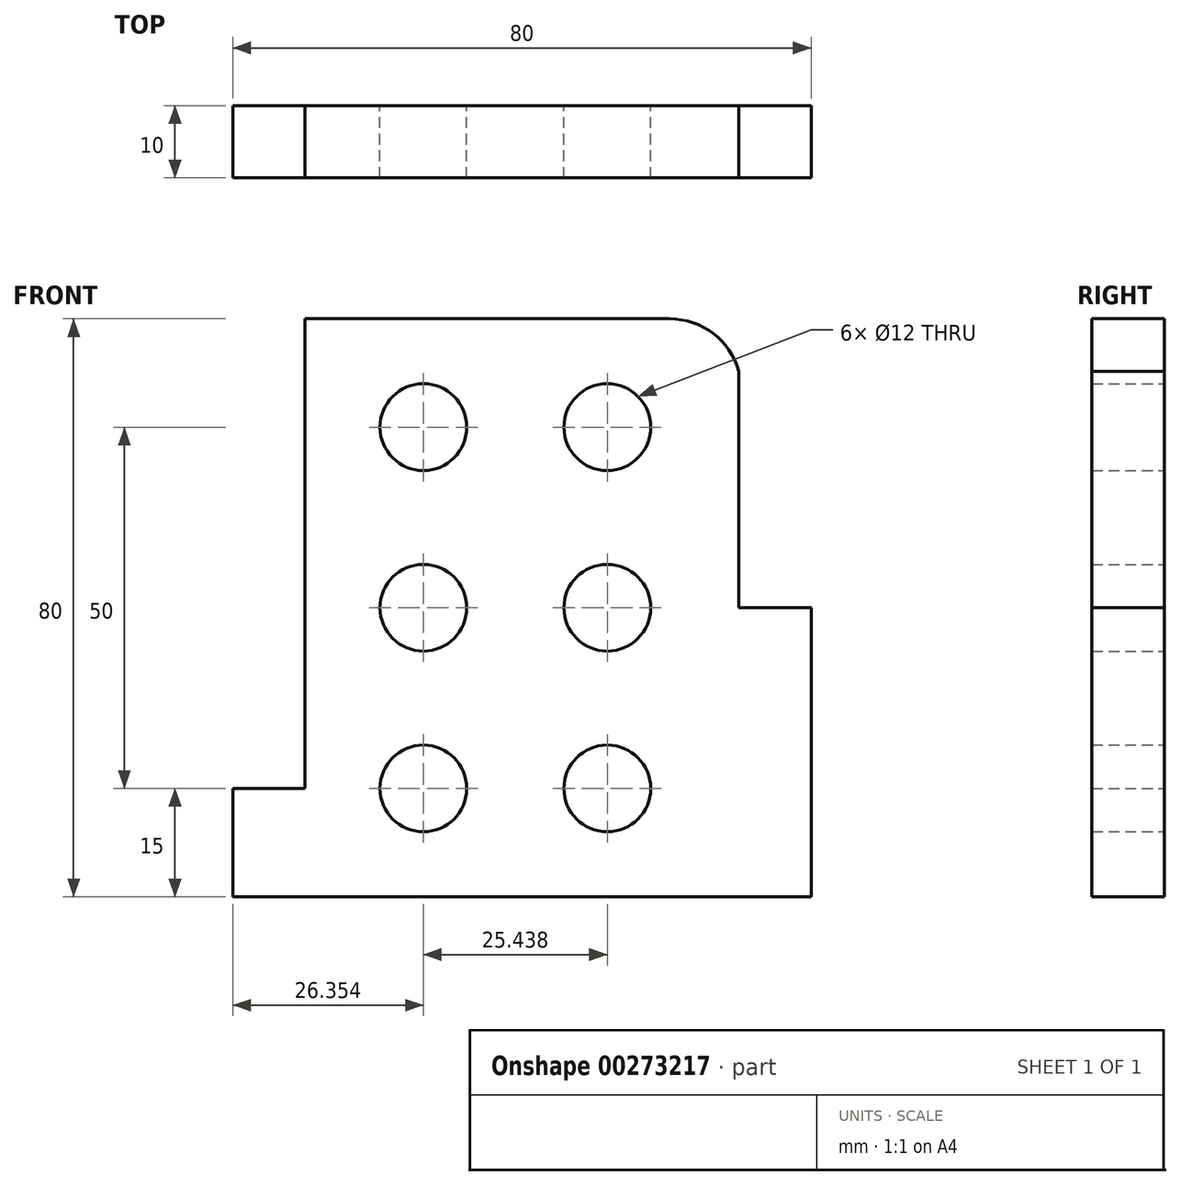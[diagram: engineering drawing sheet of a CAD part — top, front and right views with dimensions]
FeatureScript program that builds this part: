
annotation { "Feature Type Name" : "Feature", "Feature Type Description" : "" }
export const myFeature = defineFeature(function(context is Context, id is Id, definition is map)
    precondition{}
    {
        {
            var Q0;
            Q0=qCreatedBy(makeId("Front.planeOp"),FACE);
            var sketch = newSketch(context, id + "F0", { "sketchPlane" : qUnion([Q0])});
            skLineSegment(sketch, "E0", {"start": v(10, 80) * mm, "end": v(10, 15) * mm});
            skLineSegment(sketch, "E1", {"start": v(10, 15) * mm, "end": v(0, 15) * mm});
            skLineSegment(sketch, "E2", {"start": v(0, 15) * mm, "end": v(0, 0) * mm});
            skLineSegment(sketch, "E3", {"start": v(70, 40) * mm, "end": v(80, 40) * mm});
            skLineSegment(sketch, "E4", {"start": v(0, 0) * mm, "end": v(80, 0) * mm});
            skLineSegment(sketch, "E5", {"start": v(80, 0) * mm, "end": v(80, 40) * mm});
            skPoint(sketch, "E6", {"position": v(26.35, 65) * mm});
            skPoint(sketch, "E7", {"position": v(51.8, 65) * mm});
            skPoint(sketch, "E8", {"position": v(51.8, 40) * mm});
            skPoint(sketch, "E9", {"position": v(26.35, 40) * mm});
            skPoint(sketch, "E10", {"position": v(26.35, 15) * mm});
            skPoint(sketch, "E11", {"position": v(51.8, 15) * mm});
            skCircle(sketch, "E12", {"center": v(26.35, 65) * mm, "radius": 6 * mm});
            skCircle(sketch, "E13", {"center": v(51.8, 65) * mm, "radius": 6 * mm});
            skCircle(sketch, "E14", {"center": v(26.35, 40) * mm, "radius": 6 * mm});
            skCircle(sketch, "E15", {"center": v(51.8, 40) * mm, "radius": 6 * mm});
            skCircle(sketch, "E16", {"center": v(26.35, 15) * mm, "radius": 6 * mm});
            skCircle(sketch, "E17", {"center": v(51.8, 15) * mm, "radius": 6 * mm});
            skPoint(sketch, "E18", {"position": v(60.42, 80) * mm});
            skPoint(sketch, "E19", {"position": v(70, 72.74) * mm});
            skArc(sketch, "E20", {"start": v(70, 72.74) * mm, "mid": v(66.42, 77.97) * mm, "end": v(60.42, 80) * mm});
            skLineSegment(sketch, "E21", {"start": v(10, 80) * mm, "end": v(60.42, 80) * mm});
            skLineSegment(sketch, "E22", {"start": v(70, 72.74) * mm, "end": v(70, 40) * mm});
            skSolve(sketch);
        }
        {
            var Q0;
            Q0 = qSketchRegion(id + "F0", true);
            extrude(context, id + "F1", {"entities" : qUnion([Q0]), "depth" : 10 * mm});
        }
    });
